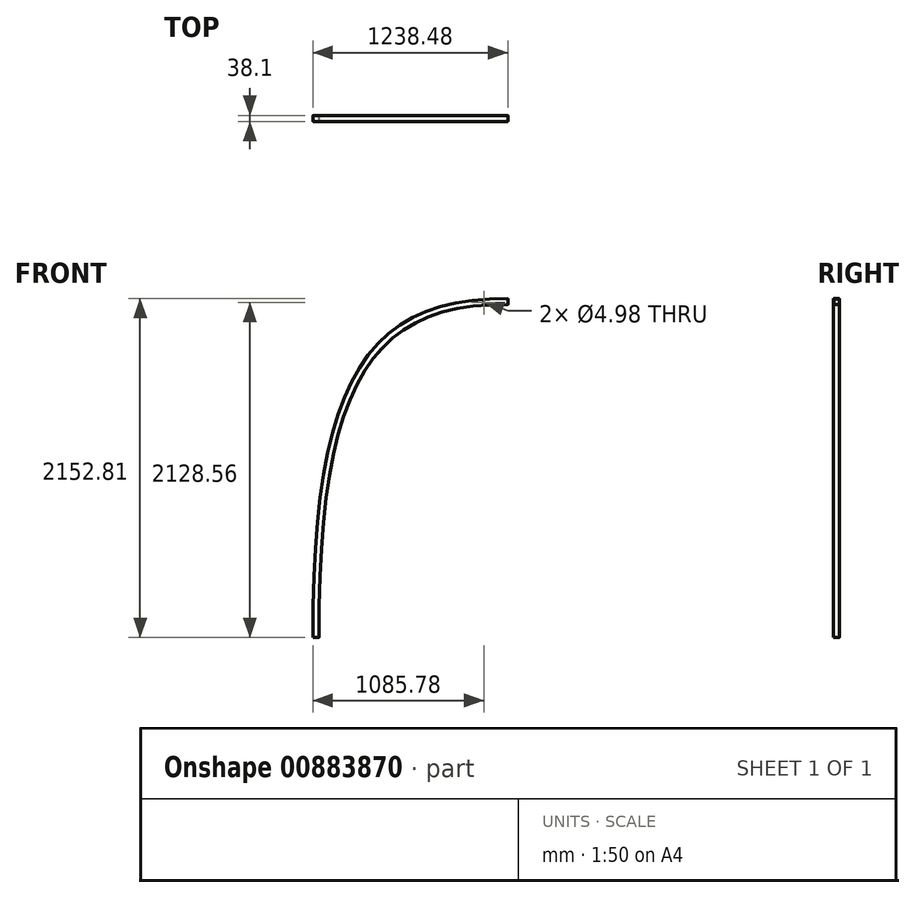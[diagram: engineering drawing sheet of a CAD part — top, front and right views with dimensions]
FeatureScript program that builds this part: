
annotation { "Feature Type Name" : "Feature", "Feature Type Description" : "" }
export const myFeature = defineFeature(function(context is Context, id is Id, definition is map)
    precondition{}
    {
        {
            var Q0;
            Q0=qCreatedBy(makeId("Top.planeOp"),FACE);
            var sketch = newSketch(context, id + "F0", { "sketchPlane" : qUnion([Q0])});
            skLineSegment(sketch, "E0.bottom", {"start": v(-17.05, 19.05) * mm, "end": v(17.05, 19.05) * mm});
            skLineSegment(sketch, "E0.top", {"start": v(-17.05, -19.05) * mm, "end": v(17.05, -19.05) * mm});
            skLineSegment(sketch, "E0.left", {"start": v(-19.05, 17.05) * mm, "end": v(-19.05, -17.05) * mm});
            skLineSegment(sketch, "E0.right", {"start": v(19.05, 17.05) * mm, "end": v(19.05, -17.05) * mm});
            skPoint(sketch, "E0.middle", {"position": v(0, 0) * mm});
            skPoint(sketch, "E1.visualSharp", {"position": v(-19.05, 19.05) * mm});
            skArc(sketch, "E1.filletArc", {"start": v(-17.05, 19.05) * mm, "mid": v(-18.46, 18.46) * mm, "end": v(-19.05, 17.05) * mm});
            skPoint(sketch, "E2.visualSharp", {"position": v(19.05, 19.05) * mm});
            skArc(sketch, "E2.filletArc", {"start": v(19.05, 17.05) * mm, "mid": v(18.46, 18.46) * mm, "end": v(17.05, 19.05) * mm});
            skPoint(sketch, "E3.visualSharp", {"position": v(19.05, -19.05) * mm});
            skArc(sketch, "E3.filletArc", {"start": v(17.05, -19.05) * mm, "mid": v(18.46, -18.46) * mm, "end": v(19.05, -17.05) * mm});
            skPoint(sketch, "E4.visualSharp", {"position": v(-19.05, -19.05) * mm});
            skArc(sketch, "E4.filletArc", {"start": v(-19.05, -17.05) * mm, "mid": v(-18.46, -18.46) * mm, "end": v(-17.05, -19.05) * mm});
            skLineSegment(sketch, "E5.0", {"start": v(-17.46, -17.46) * mm, "end": v(17.46, -17.46) * mm});
            skLineSegment(sketch, "E5.1", {"start": v(-17.46, 17.46) * mm, "end": v(-17.46, -17.46) * mm});
            skLineSegment(sketch, "E5.2", {"start": v(-17.46, 17.46) * mm, "end": v(17.46, 17.46) * mm});
            skLineSegment(sketch, "E5.3", {"start": v(17.46, 17.46) * mm, "end": v(17.46, -17.46) * mm});
            skSolve(sketch);
        }
        {
            var Q0;
            Q0=qCreatedBy(makeId("Front.planeOp"),FACE);
            var sketch = newSketch(context, id + "F1", { "sketchPlane" : qUnion([Q0])});
            skFitSpline(sketch, "E6", {"points": [v(0, 0) * mm, v(1219.2, 2133.6) * mm], "startDerivative": vector(0, 4711.7) * mm, "endDerivative": vector(2738.63, -33.4) * mm});
            skSolve(sketch);
        }
        {
            var Q0;
            Q0=makeQuery(id+"F0.imprint","IMPRINT",FACE,{"disambiguationData":[TD([[makeQuery(id+"F0.imprint","IMPRINT",EDGE,{"derivedFrom":sQuery(id+"F0.wireOp",EDGE,"E0.bottom")}),-1.0]])]});
            var Q1;
            Q1=sQuery(id+"F1.wireOp",EDGE,"E6");
            sweep(context, id + "F2", {"profiles" : qUnion([Q0]), "path" : qUnion([Q1])});
        }
        {
            var Q0;
            Q0=makeQuery(id+"F2.opSweep","SWEPT_FACE",FACE,{"disambiguationData":[OSD([sQuery(id+"F0.wireOp",EDGE,"E0.bottom"),sQuery(id+"F1.wireOp",EDGE,"E6")])]});
            var sketch = newSketch(context, id + "F3", { "sketchPlane" : qUnion([Q0])});
            skPoint(sketch, "E7", {"position": v(-1066.73, 2128.56) * mm});
            skSolve(sketch);
        }
        {
            var Q0;
            Q0=sQuery(id+"F3.wireOp",VERTEX,"E7");
            var Q1;
            Q1=makeQuery(id+"F2.opSweep","SWEPT_BODY",BODY,{"disambiguationData":[OSD([sQuery(id+"F0.wireOp",EDGE,"E0.bottom"),sQuery(id+"F0.wireOp",EDGE,"E0.top"),sQuery(id+"F0.wireOp",EDGE,"E0.left"),sQuery(id+"F0.wireOp",EDGE,"E0.right"),sQuery(id+"F0.wireOp",EDGE,"E1.filletArc"),sQuery(id+"F0.wireOp",EDGE,"E2.filletArc"),sQuery(id+"F0.wireOp",EDGE,"E3.filletArc"),sQuery(id+"F0.wireOp",EDGE,"E4.filletArc"),sQuery(id+"F0.wireOp",EDGE,"E5.0"),sQuery(id+"F0.wireOp",EDGE,"E5.1"),sQuery(id+"F0.wireOp",EDGE,"E5.2"),sQuery(id+"F0.wireOp",EDGE,"E5.3"),sQuery(id+"F1.wireOp",EDGE,"E6")])]});
            hole(context, id + "F4", {"style" : HoleStyle.SIMPLE, "endStyle" : HoleEndStyle.THROUGH, "standardTappedOrClearance" : lookupTablePath({ "fit" : "Normal (ASME)", "standard" : "ANSI", "size" : "#8", "type" : "Clearance" }), "standardBlindInLast" : lookupTablePath({ "fit" : "Normal", "standard" : "ANSI", "size" : "#8", "type" : "Clearance" }), "holeDiameter" : 4.98 * mm, "majorDiameter" : 6.1 * mm, "isTappedThrough" : true, "tappedDepth" : 12.2 * mm, "tapClearance" : 3, "locations" : qUnion([Q0]), "scope" : qUnion([Q1]), "startStyle" : HoleStartStyle.PART});
        }
    });
